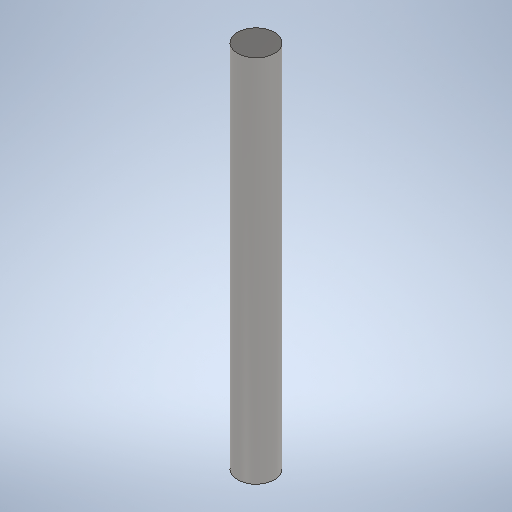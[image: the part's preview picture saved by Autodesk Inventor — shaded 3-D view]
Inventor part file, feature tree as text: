
AUTODESK INVENTOR PART (.ipt)
format: ipt  version: 2025.1 (Build 291241000, 241)  size: 227,328 bytes
history: native  units: mm
features: extrude x1, sketch x1
ambient origin geometry x8: Origin, YZ Plane, XZ Plane, XY Plane, X Axis, Y Axis, Z Axis, Center Point
bodies: Solid1 (feature_tree)
feature tree (2):
  extrude  "Extrusion1"  TaperAngle=0.0deg  [1 undecoded]
  sketch  "Sketch1"  dims[d0=8.0mm d2=0.0mm]
note: 1 required parameter value undecoded (feature->parameter linkage not recoverable at this tier; creation-order binding heuristic only, values carry confidence <= 0.55)
